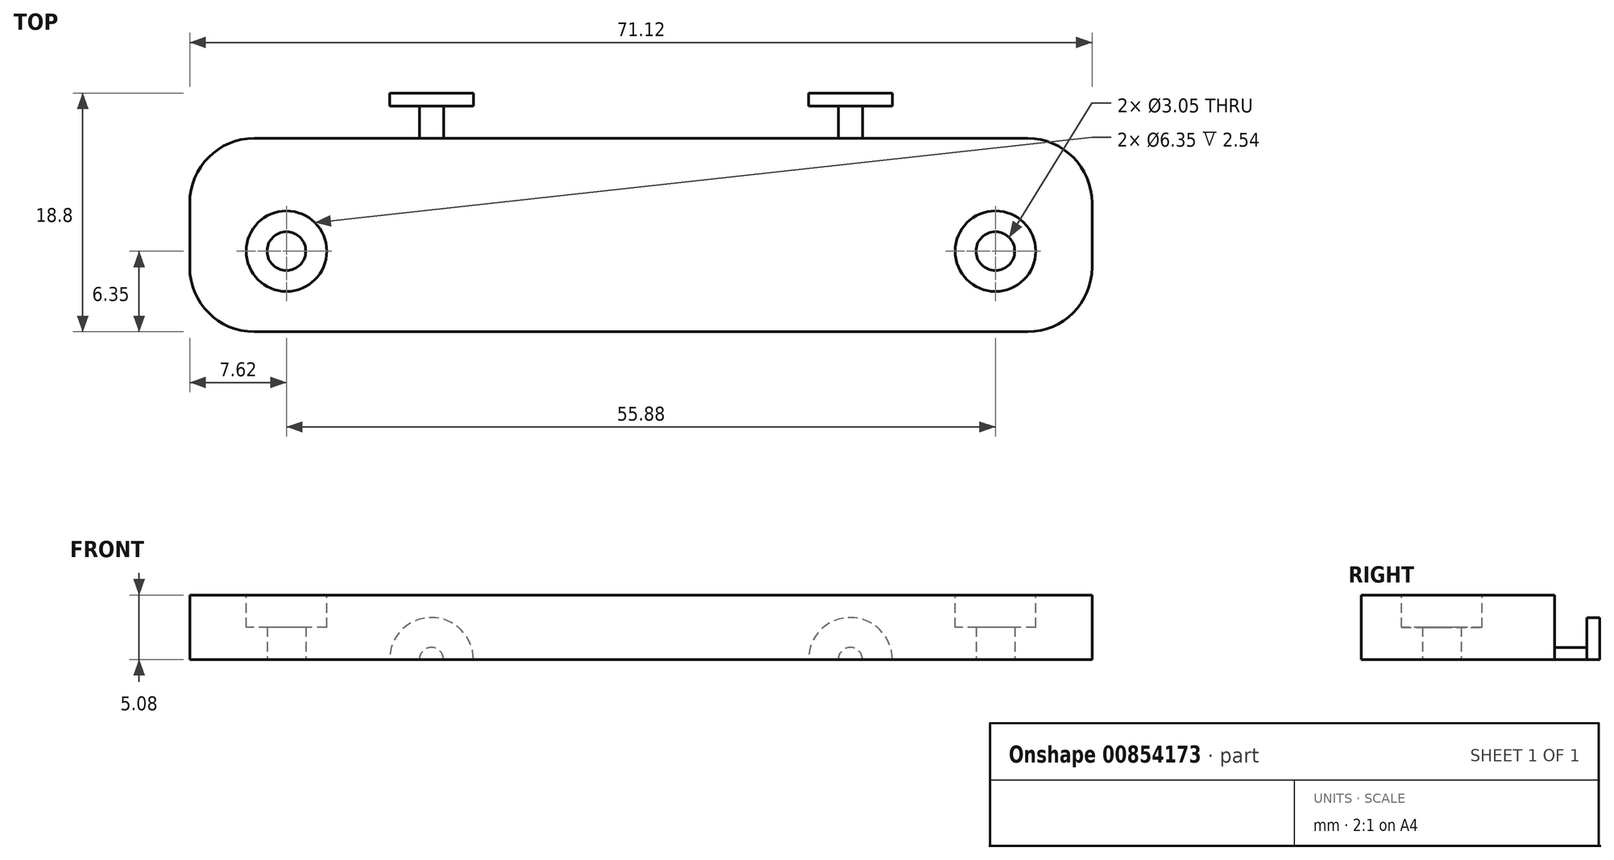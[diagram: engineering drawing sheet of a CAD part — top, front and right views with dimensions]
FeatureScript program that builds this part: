
annotation { "Feature Type Name" : "Feature", "Feature Type Description" : "" }
export const myFeature = defineFeature(function(context is Context, id is Id, definition is map)
    precondition{}
    {
        {
            var Q0;
            Q0=qCreatedBy(makeId("Top.planeOp"),FACE);
            var sketch = newSketch(context, id + "F0", { "sketchPlane" : qUnion([Q0])});
            skLineSegment(sketch, "E0", {"start": v(7.62, 0) * mm, "end": v(7.62, 6.35) * mm, "construction": true});
            skLineSegment(sketch, "E1", {"start": v(7.62, 6.35) * mm, "end": v(63.5, 6.35) * mm, "construction": true});
            skLineSegment(sketch, "E2", {"start": v(63.5, 6.35) * mm, "end": v(63.5, 0) * mm, "construction": true});
            skCircle(sketch, "E3", {"center": v(7.62, 6.35) * mm, "radius": 1.52 * mm});
            skCircle(sketch, "E4", {"center": v(63.5, 6.35) * mm, "radius": 1.52 * mm});
            skLineSegment(sketch, "E5", {"start": v(0, 0) * mm, "end": v(71.12, 0) * mm});
            skLineSegment(sketch, "E6", {"start": v(71.12, 0) * mm, "end": v(71.12, 15.24) * mm});
            skLineSegment(sketch, "E7", {"start": v(71.12, 15.24) * mm, "end": v(0, 15.24) * mm});
            skLineSegment(sketch, "E8", {"start": v(0, 15.24) * mm, "end": v(0, 0) * mm});
            skLineSegment(sketch, "E9", {"start": v(35.56, 24.03) * mm, "end": v(35.56, -12.78) * mm, "construction": true});
            skPoint(sketch, "E9.startSnap0", {"position": v(35.56, 15.24) * mm});
            skLineSegment(sketch, "E10", {"start": v(52.07, 24.03) * mm, "end": v(52.07, -12.78) * mm, "construction": true});
            skLineSegment(sketch, "E11", {"start": v(19.05, 24.03) * mm, "end": v(19.05, -12.78) * mm, "construction": true});
            skLineSegment(sketch, "E12", {"start": v(20, 15.24) * mm, "end": v(20, 17.78) * mm});
            skLineSegment(sketch, "E13", {"start": v(20, 17.78) * mm, "end": v(22.35, 17.78) * mm});
            skLineSegment(sketch, "E14", {"start": v(22.35, 17.78) * mm, "end": v(22.35, 18.8) * mm});
            skLineSegment(sketch, "E15", {"start": v(22.35, 18.8) * mm, "end": v(19.05, 18.8) * mm});
            skLineSegment(sketch, "E16", {"start": v(19.05, 18.8) * mm, "end": v(19.05, 15.24) * mm});
            skLineSegment(sketch, "E17", {"start": v(53.02, 15.24) * mm, "end": v(53.02, 17.78) * mm});
            skLineSegment(sketch, "E18", {"start": v(53.02, 17.78) * mm, "end": v(55.37, 17.78) * mm});
            skLineSegment(sketch, "E19", {"start": v(55.37, 17.78) * mm, "end": v(55.37, 18.8) * mm});
            skLineSegment(sketch, "E20", {"start": v(55.37, 18.8) * mm, "end": v(52.07, 18.8) * mm});
            skLineSegment(sketch, "E21", {"start": v(52.07, 18.8) * mm, "end": v(52.07, 15.24) * mm});
            skSolve(sketch);
        }
        {
            var Q0;
            Q0=makeQuery(id+"F0.imprint","IMPRINT",FACE,{"disambiguationData":[TD([[makeQuery(id+"F0.imprint","IMPRINT",EDGE,{"derivedFrom":sQuery(id+"F0.wireOp",EDGE,"E3")}),-1.0]])]});
            extrude(context, id + "F1", {"entities" : qUnion([Q0]), "depth" : 5.08 * mm, "offsetDistance" : 25.4 * mm});
        }
        {
            var Q0;
            {var subQ0=sQuery(id+"F0.wireOp",EDGE,"E12");Q0=makeQuery(id+"F0.imprint","IMPRINT",FACE,{"disambiguationData":[TD([[makeQuery(id+"F0.imprint","IMPRINT",EDGE,{"derivedFrom":subQ0}),1.0]])]});}
            var Q1;
            Q1=sQuery(id+"F0.wireOp",EDGE,"E11");
            revolve(context, id + "F2", {"operationType" : NewBodyOperationType.ADD, "surfaceOperationType" : NewSurfaceOperationType.NEW, "entities" : qUnion([Q0]), "axis" : qUnion([Q1]), "revolveType" : RevolveType.ONE_DIRECTION, "angle" : 180 * degree});
        }
        {
            var Q0;
            {var subQ0=sQuery(id+"F0.wireOp",EDGE,"E17");Q0=makeQuery(id+"F0.imprint","IMPRINT",FACE,{"disambiguationData":[TD([[makeQuery(id+"F0.imprint","IMPRINT",EDGE,{"derivedFrom":subQ0}),1.0]])]});}
            var Q1;
            Q1=sQuery(id+"F0.wireOp",EDGE,"E10");
            revolve(context, id + "F3", {"operationType" : NewBodyOperationType.ADD, "surfaceOperationType" : NewSurfaceOperationType.NEW, "entities" : qUnion([Q0]), "axis" : qUnion([Q1]), "revolveType" : RevolveType.ONE_DIRECTION, "angle" : 180 * degree});
        }
        {
            var Q0;
            Q0=makeQuery(id+"F1.opExtrude","CAP_FACE",FACE,{"disambiguationData":[OSD([sQuery(id+"F0.wireOp",EDGE,"E3"),sQuery(id+"F0.wireOp",EDGE,"E4"),sQuery(id+"F0.wireOp",EDGE,"E5"),sQuery(id+"F0.wireOp",EDGE,"E6"),sQuery(id+"F0.wireOp",EDGE,"E7"),sQuery(id+"F0.wireOp",EDGE,"E8")])],"isStart":false});
            var sketch = newSketch(context, id + "F4", { "sketchPlane" : qUnion([Q0])});
            skCircle(sketch, "E22", {"center": v(7.62, 6.35) * mm, "radius": 3.18 * mm});
            skCircle(sketch, "E23", {"center": v(63.5, 6.35) * mm, "radius": 3.18 * mm});
            skSolve(sketch);
        }
        {
            var Q0;
            Q0=makeQuery(id+"F4.imprint","IMPRINT",FACE,{"disambiguationData":[TD([[makeQuery(id+"F4.imprint","IMPRINT",EDGE,{"derivedFrom":sQuery(id+"F4.wireOp",EDGE,"E22")}),1.0]])]});
            var Q1;
            Q1=makeQuery(id+"F4.imprint","IMPRINT",FACE,{"disambiguationData":[TD([[makeQuery(id+"F4.imprint","IMPRINT",EDGE,{"derivedFrom":sQuery(id+"F4.wireOp",EDGE,"E23")}),1.0]])]});
            extrude(context, id + "F5", {"entities" : qUnion([Q0, Q1]), "operationType" : NewBodyOperationType.REMOVE, "oppositeDirection" : true, "depth" : 2.54 * mm, "offsetDistance" : 25.4 * mm});
        }
        {
            var Q0;
            Q0=makeQuery(id+"F1.opExtrude","SWEPT_EDGE",EDGE,{"disambiguationData":[OSD([sQuery(id+"F0.wireOp",EDGE,"E6"),sQuery(id+"F0.wireOp",EDGE,"E7")])]});
            var Q1;
            Q1=makeQuery(id+"F1.opExtrude","SWEPT_EDGE",EDGE,{"disambiguationData":[OSD([sQuery(id+"F0.wireOp",EDGE,"E5"),sQuery(id+"F0.wireOp",EDGE,"E6")])]});
            var Q2;
            Q2=makeQuery(id+"F1.opExtrude","SWEPT_EDGE",EDGE,{"disambiguationData":[OSD([sQuery(id+"F0.wireOp",EDGE,"E7"),sQuery(id+"F0.wireOp",EDGE,"E8")])]});
            var Q3;
            Q3=makeQuery(id+"F1.opExtrude","SWEPT_EDGE",EDGE,{"disambiguationData":[OSD([sQuery(id+"F0.wireOp",EDGE,"E5"),sQuery(id+"F0.wireOp",EDGE,"E8")])]});
            fillet(context, id + "F6", {"entities" : qUnion([Q0, Q1, Q2, Q3]), "radius" : 5.08 * mm, "tangentPropagation" : true, "allowEdgeOverflow" : false});
        }
    });
